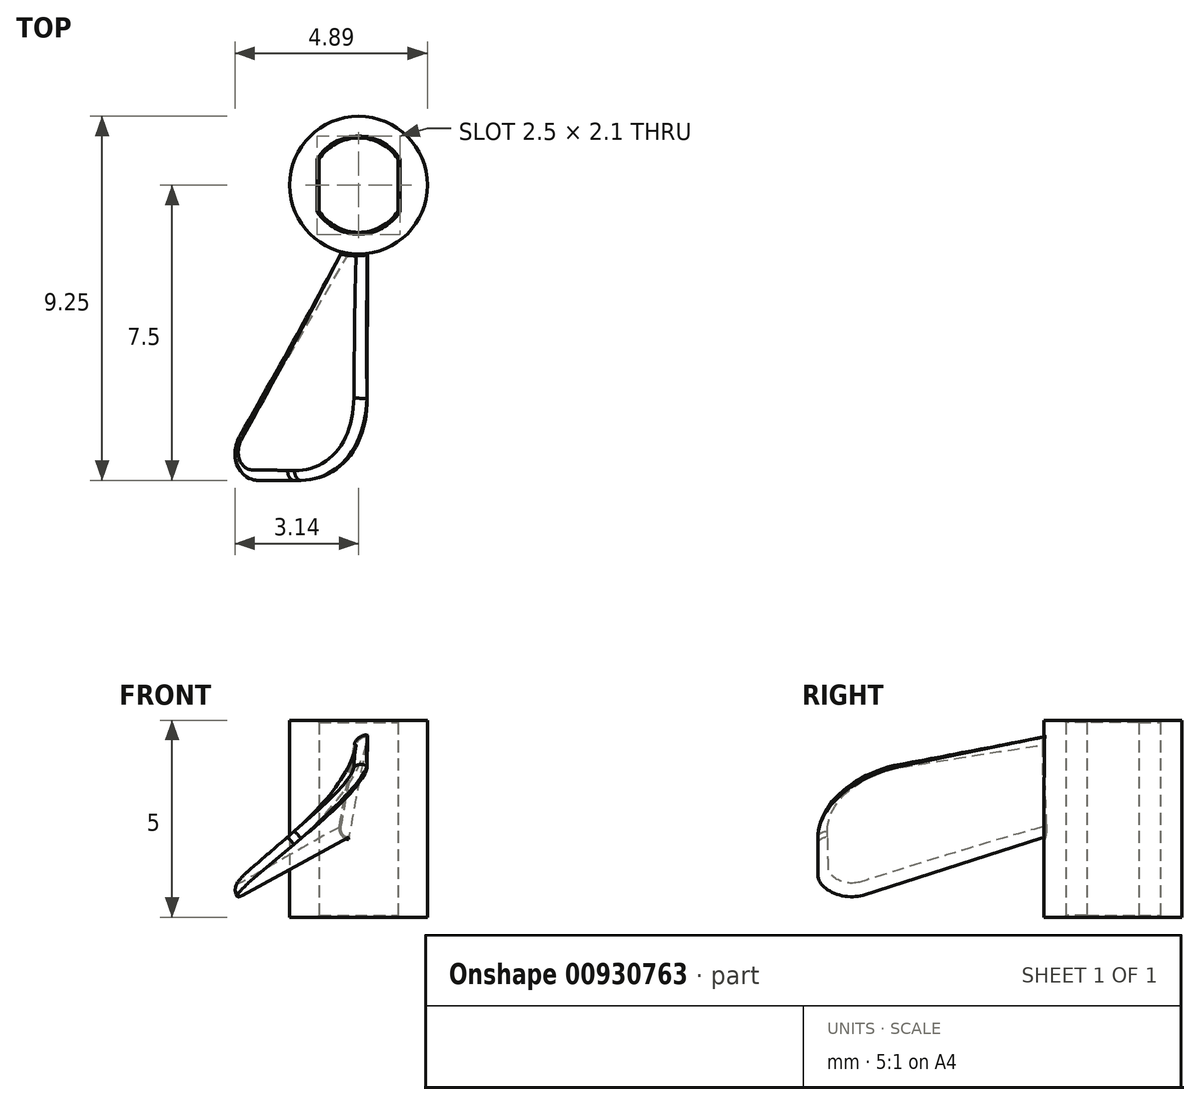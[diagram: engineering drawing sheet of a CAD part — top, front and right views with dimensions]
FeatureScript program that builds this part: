
annotation { "Feature Type Name" : "Feature", "Feature Type Description" : "" }
export const myFeature = defineFeature(function(context is Context, id is Id, definition is map)
    precondition{}
    {
        {
            var Q0;
            Q0=qCreatedBy(makeId("Top.planeOp"),FACE);
            var sketch = newSketch(context, id + "F0", { "sketchPlane" : qUnion([Q0])});
            skCircle(sketch, "E0", {"center": v(0, 0) * mm, "radius": 2.4 * mm});
            skLineSegment(sketch, "E1", {"start": v(-2, 1.33) * mm, "end": v(2, 1.33) * mm});
            skLineSegment(sketch, "E2", {"start": v(-2, -1.33) * mm, "end": v(2, -1.33) * mm});
            skLineSegment(sketch, "E3", {"start": v(-2, 1.33) * mm, "end": v(-2, -1.33) * mm});
            skLineSegment(sketch, "E4", {"start": v(2, 1.33) * mm, "end": v(2, -1.33) * mm});
            skCircle(sketch, "E5", {"center": v(0, 0) * mm, "radius": 3.5 * mm});
            skSolve(sketch);
        }
        {
            var Q0;
            Q0=makeQuery(id+"F0.imprint","IMPRINT",FACE,{"disambiguationData":[TD([[makeQuery(id+"F0.imprint","IMPRINT",EDGE,{"derivedFrom":sQuery(id+"F0.wireOp",EDGE,"E5")}),1.0]])]});
            var Q1;
            {var subQ0=sQuery(id+"F0.wireOp",EDGE,"E4");Q1=makeQuery(id+"F0.imprint","IMPRINT",FACE,{"disambiguationData":[TD([[makeQuery(id+"F0.imprint","IMPRINT",EDGE,{"derivedFrom":subQ0}),1.0]])]});}
            var Q2;
            {var subQ0=sQuery(id+"F0.wireOp",EDGE,"E3");Q2=makeQuery(id+"F0.imprint","IMPRINT",FACE,{"disambiguationData":[TD([[makeQuery(id+"F0.imprint","IMPRINT",EDGE,{"derivedFrom":subQ0}),-1.0]])]});}
            extrude(context, id + "F1", {"entities" : qUnion([Q0, Q1, Q2]), "depth" : 10 * mm, "offsetDistance" : 25 * mm});
        }
        {
            var Q0;
            Q0=qCreatedBy(makeId("Front.planeOp"),FACE);
            cPlane(context, id + "F2", {"entities" : qUnion([Q0]), "cplaneType" : CPlaneType.OFFSET, "offset" : 15 * mm, "width" : 150 * mm, "height" : 150 * mm});
        }
        {
            var Q0;
            Q0=qCreatedBy(id+"F2.planeOp",FACE);
            var sketch = newSketch(context, id + "F3", { "sketchPlane" : qUnion([Q0])});
            skLineSegment(sketch, "E6", {"start": v(-7.23, 10) * mm, "end": v(-7.23, 0) * mm, "construction": true});
            skLineSegment(sketch, "E7", {"start": v(-7.23, 0.38) * mm, "end": v(0.43, 6.81) * mm});
            skLineSegment(sketch, "E8", {"start": v(0.43, 6.81) * mm, "end": v(0.1, 7.2) * mm});
            skLineSegment(sketch, "E9", {"start": v(0.1, 7.2) * mm, "end": v(-7.55, 0.77) * mm});
            skLineSegment(sketch, "E10", {"start": v(-7.55, 0.77) * mm, "end": v(-7.23, 0.38) * mm});
            skSolve(sketch);
        }
        {
            var Q0;
            Q0=qCreatedBy(makeId("Front.planeOp"),FACE);
            cPlane(context, id + "F4", {"entities" : qUnion([Q0]), "cplaneType" : CPlaneType.OFFSET, "offset" : 2.6 * mm, "width" : 150 * mm, "height" : 150 * mm});
        }
        {
            var Q0;
            Q0=qCreatedBy(id+"F4.planeOp",FACE);
            var sketch = newSketch(context, id + "F5", { "sketchPlane" : qUnion([Q0])});
            skLineSegment(sketch, "E11", {"start": v(-0.48, 0) * mm, "end": v(-0.48, 9) * mm, "construction": true});
            skLineSegment(sketch, "E12", {"start": v(-0.48, 4.4) * mm, "end": v(-0.04, 9.39) * mm});
            skLineSegment(sketch, "E13", {"start": v(-0.04, 9.39) * mm, "end": v(0.45, 9.35) * mm});
            skLineSegment(sketch, "E14", {"start": v(0.45, 9.35) * mm, "end": v(0.02, 4.37) * mm});
            skLineSegment(sketch, "E15", {"start": v(0.02, 4.37) * mm, "end": v(-0.48, 4.4) * mm});
            skSolve(sketch);
        }
        {
            var Q1;
            Q1=qSketchRegion(id+"F3",true);
            var Q2;
            Q2=qSketchRegion(id+"F5",true);
            loft(context, id + "F6", {"operationType" : NewBodyOperationType.ADD, "sheetProfilesArray" : [{ "sheetProfileEntities" : qUnion([Q1]) }, { "sheetProfileEntities" : qUnion([Q2]) }]});
        }
        {
            var Q0;
            Q0=makeQuery(id+"F26cwcx8InL0C1a_1.2.F6.opLoft","MID_CAP_EDGE",EDGE,{"disambiguationData":[OSD([sQuery(id+"F3.wireOp",EDGE,"E7"),sQuery(id+"F3.wireOp",EDGE,"E8"),sQuery(id+"F3.wireOp",EDGE,"E9")])],"capPos":0.0});
            var Q1;
            Q1=makeQuery(id+"F6.opLoft","MID_CAP_EDGE",EDGE,{"disambiguationData":[OSD([sQuery(id+"F3.wireOp",EDGE,"E7"),sQuery(id+"F3.wireOp",EDGE,"E8"),sQuery(id+"F3.wireOp",EDGE,"E9")])],"capPos":0.0});
            var Q2;
            Q2=makeQuery(id+"F26cwcx8InL0C1a_1.1.F6.opLoft","MID_CAP_EDGE",EDGE,{"disambiguationData":[OSD([sQuery(id+"F3.wireOp",EDGE,"E7"),sQuery(id+"F3.wireOp",EDGE,"E8"),sQuery(id+"F3.wireOp",EDGE,"E9")])],"capPos":0.0});
            var Q3;
            Q3=makeQuery(id+"F26cwcx8InL0C1a_1.4.F6.opLoft","MID_CAP_EDGE",EDGE,{"disambiguationData":[OSD([sQuery(id+"F3.wireOp",EDGE,"E7"),sQuery(id+"F3.wireOp",EDGE,"E8"),sQuery(id+"F3.wireOp",EDGE,"E9")])],"capPos":0.0});
            var Q4;
            Q4=makeQuery(id+"F26cwcx8InL0C1a_1.3.F6.opLoft","MID_CAP_EDGE",EDGE,{"disambiguationData":[OSD([sQuery(id+"F3.wireOp",EDGE,"E7"),sQuery(id+"F3.wireOp",EDGE,"E8"),sQuery(id+"F3.wireOp",EDGE,"E9")])],"capPos":0.0});
            fillet(context, id + "F7", {"entities" : qUnion([Q0, Q1, Q2, Q3, Q4]), "radius" : 5 * mm, "tangentPropagation" : true, "allowEdgeOverflow" : false});
        }
        {
            var Q0;
            Q0=makeQuery(id+"F6.opLoft","MID_CAP_EDGE",EDGE,{"disambiguationData":[OSD([sQuery(id+"F3.wireOp",EDGE,"E7"),sQuery(id+"F3.wireOp",EDGE,"E9"),sQuery(id+"F3.wireOp",EDGE,"E10")])],"capPos":0.0});
            var Q1;
            Q1=makeQuery(id+"F26cwcx8InL0C1a_1.2.F6.opLoft","MID_CAP_EDGE",EDGE,{"disambiguationData":[OSD([sQuery(id+"F3.wireOp",EDGE,"E7"),sQuery(id+"F3.wireOp",EDGE,"E9"),sQuery(id+"F3.wireOp",EDGE,"E10")])],"capPos":0.0});
            var Q2;
            Q2=makeQuery(id+"F26cwcx8InL0C1a_1.1.F6.opLoft","MID_CAP_EDGE",EDGE,{"disambiguationData":[OSD([sQuery(id+"F3.wireOp",EDGE,"E7"),sQuery(id+"F3.wireOp",EDGE,"E9"),sQuery(id+"F3.wireOp",EDGE,"E10")])],"capPos":0.0});
            var Q3;
            Q3=makeQuery(id+"F26cwcx8InL0C1a_1.4.F6.opLoft","MID_CAP_EDGE",EDGE,{"disambiguationData":[OSD([sQuery(id+"F3.wireOp",EDGE,"E7"),sQuery(id+"F3.wireOp",EDGE,"E9"),sQuery(id+"F3.wireOp",EDGE,"E10")])],"capPos":0.0});
            var Q4;
            Q4=makeQuery(id+"F26cwcx8InL0C1a_1.3.F6.opLoft","MID_CAP_EDGE",EDGE,{"disambiguationData":[OSD([sQuery(id+"F3.wireOp",EDGE,"E7"),sQuery(id+"F3.wireOp",EDGE,"E9"),sQuery(id+"F3.wireOp",EDGE,"E10")])],"capPos":0.0});
            fillet(context, id + "F8", {"entities" : qUnion([Q0, Q1, Q2, Q3, Q4]), "radius" : 1.5 * mm, "tangentPropagation" : true, "allowEdgeOverflow" : false});
        }
        {
            var Q0;
            Q0=makeQuery(id+"F26cwcx8InL0C1a_1.1.F6.opLoft","SWEPT_EDGE",EDGE,{"disambiguationData":[OSD([sQuery(id+"F3.wireOp",EDGE,"E8"),sQuery(id+"F3.wireOp",EDGE,"E9"),sQuery(id+"F5.wireOp",EDGE,"E12"),sQuery(id+"F5.wireOp",EDGE,"E13")])]});
            var Q1;
            Q1=makeQuery(id+"F6.opLoft","SWEPT_EDGE",EDGE,{"disambiguationData":[OSD([sQuery(id+"F3.wireOp",EDGE,"E8"),sQuery(id+"F3.wireOp",EDGE,"E9"),sQuery(id+"F5.wireOp",EDGE,"E12"),sQuery(id+"F5.wireOp",EDGE,"E13")])]});
            var Q2;
            Q2=makeQuery(id+"F26cwcx8InL0C1a_1.2.F6.opLoft","SWEPT_EDGE",EDGE,{"disambiguationData":[OSD([sQuery(id+"F3.wireOp",EDGE,"E8"),sQuery(id+"F3.wireOp",EDGE,"E9"),sQuery(id+"F5.wireOp",EDGE,"E12"),sQuery(id+"F5.wireOp",EDGE,"E13")])]});
            var Q3;
            Q3=makeQuery(id+"F26cwcx8InL0C1a_1.3.F6.opLoft","SWEPT_EDGE",EDGE,{"disambiguationData":[OSD([sQuery(id+"F3.wireOp",EDGE,"E8"),sQuery(id+"F3.wireOp",EDGE,"E9"),sQuery(id+"F5.wireOp",EDGE,"E12"),sQuery(id+"F5.wireOp",EDGE,"E13")])]});
            var Q4;
            Q4=makeQuery(id+"F26cwcx8InL0C1a_1.4.F6.opLoft","SWEPT_EDGE",EDGE,{"disambiguationData":[OSD([sQuery(id+"F3.wireOp",EDGE,"E8"),sQuery(id+"F3.wireOp",EDGE,"E9"),sQuery(id+"F5.wireOp",EDGE,"E12"),sQuery(id+"F5.wireOp",EDGE,"E13")])]});
            fillet(context, id + "F9", {"entities" : qUnion([Q0, Q1, Q2, Q3, Q4]), "radius" : 0.5 * mm, "tangentPropagation" : true, "allowEdgeOverflow" : false});
        }
        {
            var Q0;
            Q0=makeQuery(id+"F9.opFillet","BLEND_EDGE",EDGE,{"blendedFrom":[makeQuery(id+"F26cwcx8InL0C1a_1.1.F6.opLoft","SWEPT_EDGE",EDGE,{"disambiguationData":[OSD([sQuery(id+"F3.wireOp",EDGE,"E8"),sQuery(id+"F3.wireOp",EDGE,"E9"),sQuery(id+"F5.wireOp",EDGE,"E12"),sQuery(id+"F5.wireOp",EDGE,"E13")])]}),makeQuery(id+"F1.opExtrude","SWEPT_FACE",FACE,{"disambiguationData":[OSD([sQuery(id+"F0.wireOp",EDGE,"E5")])]})],"blendedInto":[makeQuery(id+"F1.opExtrude","SWEPT_FACE",FACE,{"disambiguationData":[OSD([sQuery(id+"F0.wireOp",EDGE,"E5")])]})]});
            var Q1;
            Q1=makeQuery(id+"F6.boolean.opBoolean","INTERSECT",EDGE,{"derivedFrom":[makeQuery(id+"F1.opExtrude","SWEPT_FACE",FACE,{"disambiguationData":[OSD([sQuery(id+"F0.wireOp",EDGE,"E5")])]}),makeQuery(id+"F6.opLoft","SWEPT_FACE",FACE,{"disambiguationData":[OSD([sQuery(id+"F3.wireOp",EDGE,"E8"),sQuery(id+"F3.wireOp",EDGE,"E9"),sQuery(id+"F3.wireOp",EDGE,"E10"),sQuery(id+"F5.wireOp",EDGE,"E12"),sQuery(id+"F5.wireOp",EDGE,"E13"),sQuery(id+"F5.wireOp",EDGE,"E15")])]})]});
            var Q2;
            Q2=makeQuery(id+"F26cwcx8InL0C1a_1.2.F6.boolean.opBoolean","INTERSECT",EDGE,{"derivedFrom":[makeQuery(id+"F1.opExtrude","SWEPT_FACE",FACE,{"disambiguationData":[OSD([sQuery(id+"F0.wireOp",EDGE,"E5")])]}),makeQuery(id+"F26cwcx8InL0C1a_1.2.F6.opLoft","SWEPT_FACE",FACE,{"disambiguationData":[OSD([sQuery(id+"F3.wireOp",EDGE,"E8"),sQuery(id+"F3.wireOp",EDGE,"E9"),sQuery(id+"F3.wireOp",EDGE,"E10"),sQuery(id+"F5.wireOp",EDGE,"E12"),sQuery(id+"F5.wireOp",EDGE,"E13"),sQuery(id+"F5.wireOp",EDGE,"E15")])]})]});
            var Q3;
            Q3=makeQuery(id+"F26cwcx8InL0C1a_1.4.F6.boolean.opBoolean","INTERSECT",EDGE,{"derivedFrom":[makeQuery(id+"F1.opExtrude","SWEPT_FACE",FACE,{"disambiguationData":[OSD([sQuery(id+"F0.wireOp",EDGE,"E5")])]}),makeQuery(id+"F26cwcx8InL0C1a_1.4.F6.opLoft","SWEPT_FACE",FACE,{"disambiguationData":[OSD([sQuery(id+"F3.wireOp",EDGE,"E8"),sQuery(id+"F3.wireOp",EDGE,"E9"),sQuery(id+"F3.wireOp",EDGE,"E10"),sQuery(id+"F5.wireOp",EDGE,"E12"),sQuery(id+"F5.wireOp",EDGE,"E13"),sQuery(id+"F5.wireOp",EDGE,"E15")])]})]});
            var Q4;
            Q4=makeQuery(id+"F26cwcx8InL0C1a_1.3.F6.boolean.opBoolean","INTERSECT",EDGE,{"derivedFrom":[makeQuery(id+"F1.opExtrude","SWEPT_FACE",FACE,{"disambiguationData":[OSD([sQuery(id+"F0.wireOp",EDGE,"E5")])]}),makeQuery(id+"F26cwcx8InL0C1a_1.3.F6.opLoft","SWEPT_FACE",FACE,{"disambiguationData":[OSD([sQuery(id+"F3.wireOp",EDGE,"E8"),sQuery(id+"F3.wireOp",EDGE,"E9"),sQuery(id+"F3.wireOp",EDGE,"E10"),sQuery(id+"F5.wireOp",EDGE,"E12"),sQuery(id+"F5.wireOp",EDGE,"E13"),sQuery(id+"F5.wireOp",EDGE,"E15")])]})]});
            fillet(context, id + "F10", {"entities" : qUnion([Q0, Q1, Q2, Q3, Q4]), "radius" : 0.1 * mm, "tangentPropagation" : true, "allowEdgeOverflow" : false});
        }
        {
            var Q0;
            {var subQ0=sQuery(id+"F0.wireOp",EDGE,"E1");var subQ1=sQuery(id+"F0.wireOp",EDGE,"E0");Q0=makeQuery(id+"F1.opExtrude","CAP_EDGE",EDGE,{"disambiguationData":[OSD([subQ1]),TDD([makeQuery(id+"F0.imprint","IMPRINT",EDGE,{"disambiguationData":[TD([[makeQuery(id+"F0.imprint","INTERSECT",VERTEX,{"derivedFrom":[subQ1,subQ0,sQuery(id+"F0.wireOp",EDGE,"E3")]}),1.0]])],"derivedFrom":subQ1})])],"isStart":false});}
            var Q1;
            Q1=makeQuery(id+"F1.opExtrude","CAP_EDGE",EDGE,{"disambiguationData":[OSD([sQuery(id+"F0.wireOp",EDGE,"E3")])],"isStart":false});
            var Q2;
            {var subQ0=sQuery(id+"F0.wireOp",EDGE,"E2");var subQ1=sQuery(id+"F0.wireOp",EDGE,"E0");Q2=makeQuery(id+"F1.opExtrude","CAP_EDGE",EDGE,{"disambiguationData":[OSD([subQ1]),TDD([makeQuery(id+"F0.imprint","IMPRINT",EDGE,{"disambiguationData":[TD([[makeQuery(id+"F0.imprint","INTERSECT",VERTEX,{"derivedFrom":[subQ1,subQ0,sQuery(id+"F0.wireOp",EDGE,"E3")]}),-1.0]])],"derivedFrom":subQ1})])],"isStart":false});}
            var Q3;
            Q3=makeQuery(id+"F1.opExtrude","CAP_EDGE",EDGE,{"disambiguationData":[OSD([sQuery(id+"F0.wireOp",EDGE,"E4")])],"isStart":false});
            var Q4;
            Q4=makeQuery(id+"F1.opExtrude","CAP_EDGE",EDGE,{"disambiguationData":[OSD([sQuery(id+"F0.wireOp",EDGE,"E4")])],"isStart":true});
            var Q5;
            {var subQ0=sQuery(id+"F0.wireOp",EDGE,"E2");var subQ1=sQuery(id+"F0.wireOp",EDGE,"E0");Q5=makeQuery(id+"F1.opExtrude","CAP_EDGE",EDGE,{"disambiguationData":[OSD([subQ1]),TDD([makeQuery(id+"F0.imprint","IMPRINT",EDGE,{"disambiguationData":[TD([[makeQuery(id+"F0.imprint","INTERSECT",VERTEX,{"derivedFrom":[subQ1,subQ0,sQuery(id+"F0.wireOp",EDGE,"E3")]}),-1.0]])],"derivedFrom":subQ1})])],"isStart":true});}
            var Q6;
            Q6=makeQuery(id+"F1.opExtrude","CAP_EDGE",EDGE,{"disambiguationData":[OSD([sQuery(id+"F0.wireOp",EDGE,"E3")])],"isStart":true});
            var Q7;
            {var subQ0=sQuery(id+"F0.wireOp",EDGE,"E1");var subQ1=sQuery(id+"F0.wireOp",EDGE,"E0");Q7=makeQuery(id+"F1.opExtrude","CAP_EDGE",EDGE,{"disambiguationData":[OSD([subQ1]),TDD([makeQuery(id+"F0.imprint","IMPRINT",EDGE,{"disambiguationData":[TD([[makeQuery(id+"F0.imprint","INTERSECT",VERTEX,{"derivedFrom":[subQ1,subQ0,sQuery(id+"F0.wireOp",EDGE,"E3")]}),1.0]])],"derivedFrom":subQ1})])],"isStart":true});}
            chamfer(context, id + "F11", {"entities" : qUnion([Q0, Q1, Q2, Q3, Q4, Q5, Q6, Q7]), "width" : 0.1 * mm, "tangentPropagation" : true});
        }
        {
            var Q0;
            Q0=makeQuery(id+"F1.opExtrude","SWEPT_BODY",BODY,{"disambiguationData":[OSD([sQuery(id+"F0.wireOp",EDGE,"E0"),sQuery(id+"F0.wireOp",EDGE,"E3"),sQuery(id+"F0.wireOp",EDGE,"E4"),sQuery(id+"F0.wireOp",EDGE,"E5")])]});
            var Q1;
            Q1=qCreatedBy(makeId("Origin.pointOp"),VERTEX);
            transform(context, id + "F12", {"entities" : qUnion([Q0]), "transformType" : TransformType.SCALE_UNIFORMLY, "scale" : 0.5, "scalePoint" : qUnion([Q1]), "makeCopy" : false});
        }
    });
